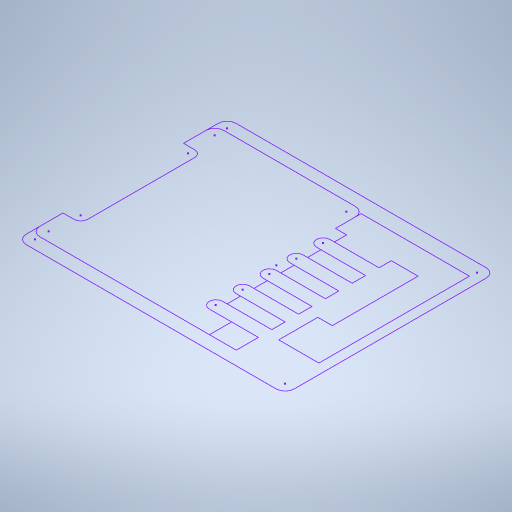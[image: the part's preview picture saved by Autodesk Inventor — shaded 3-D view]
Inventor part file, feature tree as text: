
AUTODESK INVENTOR PART (.ipt)
format: ipt  version: 2023 (Build 270158000, 158)  size: 255,488 bytes
history: native  units: in
note: dims shown in document units (in); Inventor stores cm internally (conversion verified against a paired STEP export)
features: sketch x1
ambient origin geometry x8: Origin, YZ Plane, XZ Plane, XY Plane, X Axis, Y Axis, Z Axis, Center Point
feature tree (1):
  sketch  "Sketch1"
